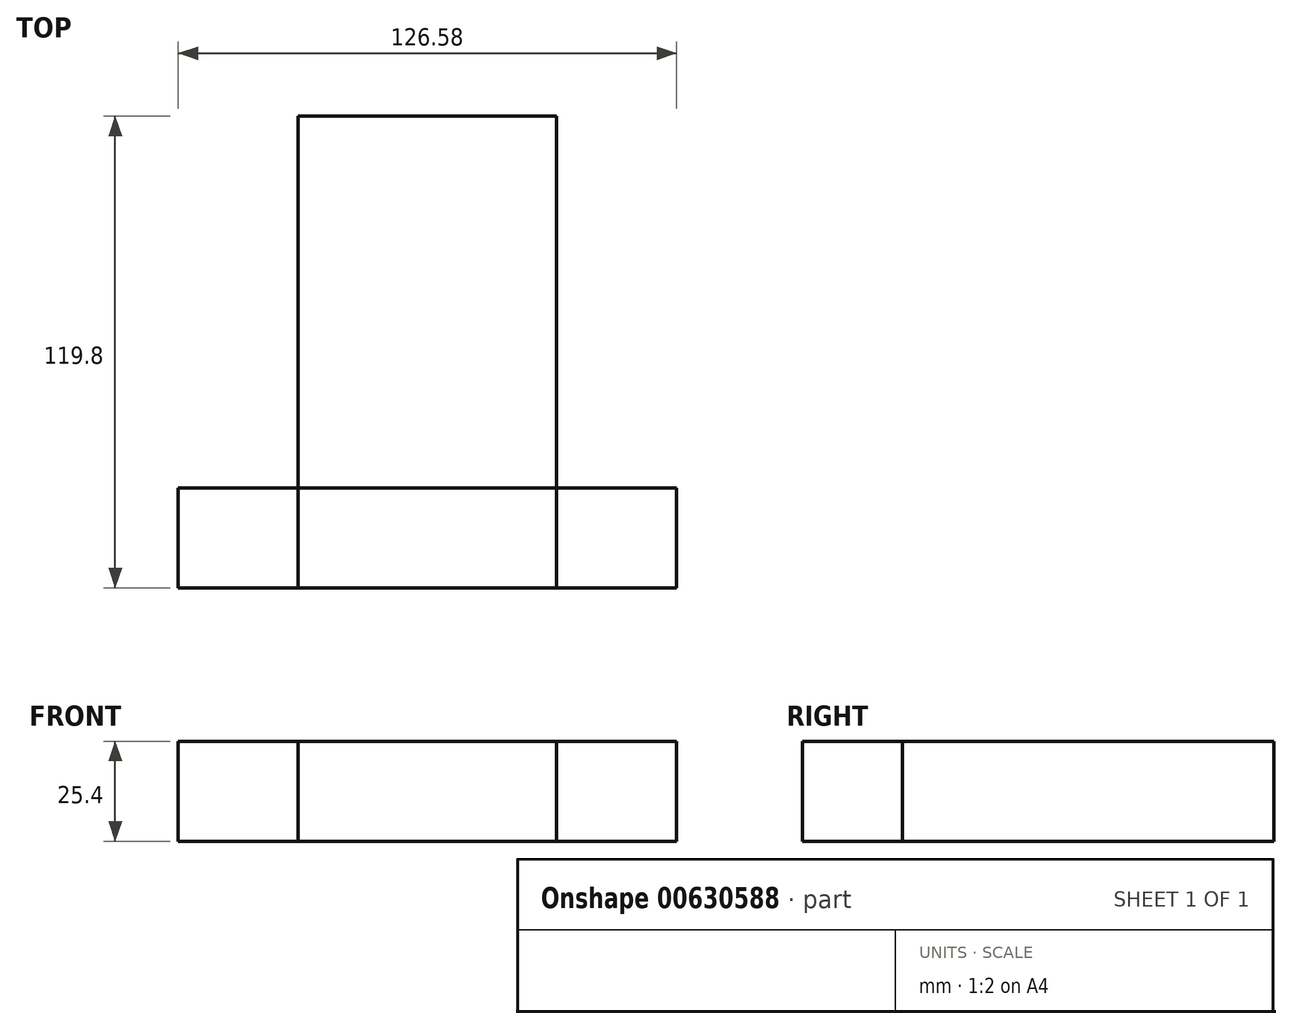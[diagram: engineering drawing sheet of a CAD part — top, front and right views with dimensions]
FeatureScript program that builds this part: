
annotation { "Feature Type Name" : "Feature", "Feature Type Description" : "" }
export const myFeature = defineFeature(function(context is Context, id is Id, definition is map)
    precondition{}
    {
        {
            var Q0;
            Q0=qCreatedBy(makeId("Top.planeOp"),FACE);
            var sketch = newSketch(context, id + "F0", { "sketchPlane" : qUnion([Q0])});
            skLineSegment(sketch, "E0.bottom", {"start": v(-40.44, -45.04) * mm, "end": v(25.18, -45.04) * mm});
            skLineSegment(sketch, "E0.top", {"start": v(-40.44, 49.36) * mm, "end": v(25.18, 49.36) * mm});
            skLineSegment(sketch, "E0.left", {"start": v(-40.44, -45.04) * mm, "end": v(-40.44, 49.36) * mm});
            skLineSegment(sketch, "E0.right", {"start": v(25.18, -45.04) * mm, "end": v(25.18, 49.36) * mm});
            skSolve(sketch);
        }
        {
            var Q0;
            Q0=makeQuery(id+"F0.imprint","IMPRINT",FACE,{"disambiguationData":[TD([[makeQuery(id+"F0.imprint","IMPRINT",EDGE,{"derivedFrom":sQuery(id+"F0.wireOp",EDGE,"E0.bottom")}),1.0]])]});
            extrude(context, id + "F1", {"entities" : qUnion([Q0]), "depth" : 25.4 * mm, "offsetDistance" : 25.4 * mm});
        }
        {
            var Q0;
            Q0=makeQuery(id+"F1.opExtrude","SWEPT_FACE",FACE,{"disambiguationData":[OSD([sQuery(id+"F0.wireOp",EDGE,"E0.bottom")])]});
            var sketch = newSketch(context, id + "F2", { "sketchPlane" : qUnion([Q0])});
            skLineSegment(sketch, "E1", {"start": v(-40.44, 25.4) * mm, "end": v(-70.92, 25.4) * mm});
            skLineSegment(sketch, "E2", {"start": v(-30.16, 16.55) * mm, "end": v(-35.8, 16.55) * mm});
            skLineSegment(sketch, "E3", {"start": v(-70.92, 25.4) * mm, "end": v(-70.92, 0) * mm});
            skLineSegment(sketch, "E4", {"start": v(25.18, 25.4) * mm, "end": v(55.66, 25.4) * mm});
            skLineSegment(sketch, "E5", {"start": v(55.66, 25.4) * mm, "end": v(55.66, 0) * mm});
            skLineSegment(sketch, "E6", {"start": v(55.66, 0) * mm, "end": v(25.18, 0) * mm});
            skLineSegment(sketch, "E7", {"start": v(-70.92, 0) * mm, "end": v(-40.44, 0) * mm});
            skSolve(sketch);
        }
        {
            var Q0;
            Q0=makeQuery(id+"F2.imprint","IMPRINT",FACE,{"disambiguationData":[TD([[makeQuery(id+"F2.imprint","IMPRINT",EDGE,{"derivedFrom":sQuery(id+"F2.wireOp",EDGE,"E1")}),1.0]])]});
            var Q1;
            Q1=makeQuery(id+"F2.imprint","IMPRINT",FACE,{"disambiguationData":[TD([[makeQuery(id+"F2.imprint","IMPRINT",EDGE,{"derivedFrom":sQuery(id+"F2.wireOp",EDGE,"E4")}),-1.0]])]});
            extrude(context, id + "F3", {"entities" : qUnion([Q0, Q1]), "depth" : 25.4 * mm, "offsetDistance" : 25.4 * mm});
        }
        {
            var Q0;
            Q0=makeQuery(id+"F1.opExtrude","SWEPT_FACE",FACE,{"disambiguationData":[OSD([sQuery(id+"F0.wireOp",EDGE,"E0.bottom")])]});
            var sketch = newSketch(context, id + "F4", { "sketchPlane" : qUnion([Q0])});
            skLineSegment(sketch, "E8", {"start": v(-40.44, 25.4) * mm, "end": v(25.18, 25.4) * mm});
            skLineSegment(sketch, "E9", {"start": v(-40.44, 0) * mm, "end": v(25.18, 0) * mm});
            skSolve(sketch);
        }
        {
            var Q0;
            Q0=makeQuery(id+"F4.imprint","IMPRINT",FACE,{"disambiguationData":[TD([[makeQuery(id+"F4.imprint","IMPRINT",EDGE,{"derivedFrom":sQuery(id+"F4.wireOp",EDGE,"E8")}),-1.0]])]});
            extrude(context, id + "F5", {"entities" : qUnion([Q0]), "depth" : 25.4 * mm, "offsetDistance" : 25.4 * mm});
        }
    });
